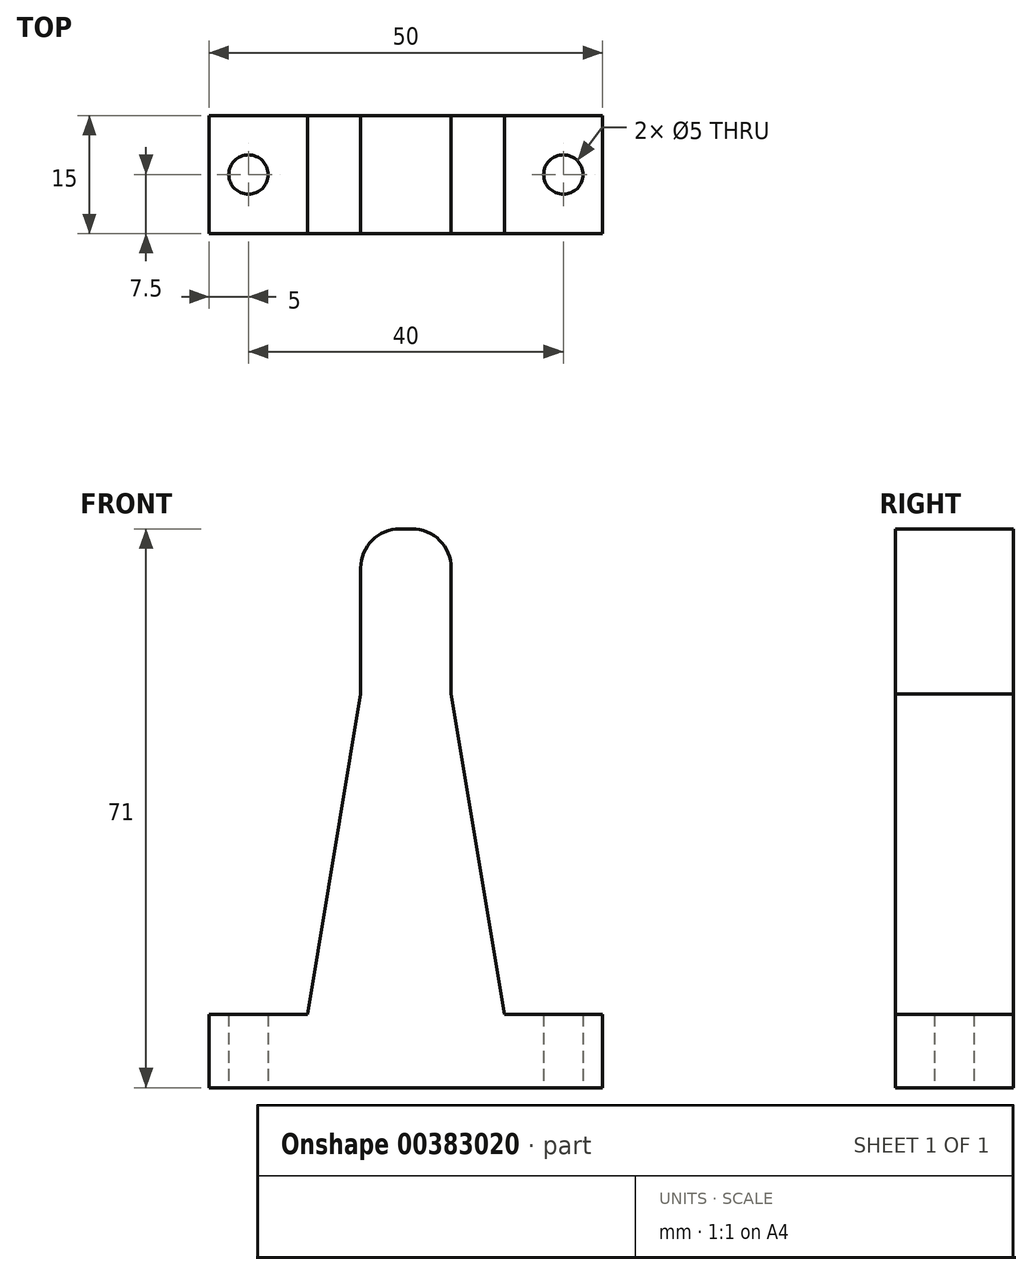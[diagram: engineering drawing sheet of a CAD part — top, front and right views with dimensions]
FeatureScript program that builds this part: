
annotation { "Feature Type Name" : "Feature", "Feature Type Description" : "" }
export const myFeature = defineFeature(function(context is Context, id is Id, definition is map)
    precondition{}
    {
        {
            var Q0;
            Q0=qCreatedBy(makeId("Front.planeOp"),FACE);
            var sketch = newSketch(context, id + "F0", { "sketchPlane" : qUnion([Q0])});
            skLineSegment(sketch, "E0.bottom", {"start": v(-0.75, 71) * mm, "end": v(0.75, 71) * mm});
            skLineSegment(sketch, "E0.top", {"start": v(-12.5, 0) * mm, "end": v(12.5, 0) * mm});
            skLineSegment(sketch, "E0.left", {"start": v(-12.5, 45) * mm, "end": v(-12.5, 9.28) * mm, "construction": true});
            skLineSegment(sketch, "E0.right", {"start": v(12.5, 44.18) * mm, "end": v(12.5, 9.28) * mm, "construction": true});
            skLineSegment(sketch, "E1.bottom", {"start": v(-25, 9.28) * mm, "end": v(-12.5, 9.28) * mm});
            skLineSegment(sketch, "E1.top", {"start": v(-25, 0) * mm, "end": v(25, 0) * mm});
            skLineSegment(sketch, "E1.left", {"start": v(-25, 9.28) * mm, "end": v(-25, 0) * mm});
            skLineSegment(sketch, "E1.right", {"start": v(25, 9.28) * mm, "end": v(25, 0) * mm});
            skLineSegment(sketch, "E2.trimOffspring", {"start": v(12.5, 9.28) * mm, "end": v(25, 9.28) * mm});
            skLineSegment(sketch, "E3", {"start": v(-5.75, 66) * mm, "end": v(-5.75, 50) * mm});
            skLineSegment(sketch, "E4", {"start": v(-10.75, 45) * mm, "end": v(-12.5, 45) * mm, "construction": true});
            skLineSegment(sketch, "E5", {"start": v(5.75, 66) * mm, "end": v(5.75, 50) * mm});
            skLineSegment(sketch, "E6", {"start": v(10.75, 45) * mm, "end": v(11.68, 45) * mm, "construction": true});
            skPoint(sketch, "E7.visualSharp", {"position": v(-5.75, 45) * mm});
            skArc(sketch, "E7.filletArc", {"start": v(-10.75, 45) * mm, "mid": v(-7.21, 46.46) * mm, "end": v(-5.75, 50) * mm, "construction": true});
            skPoint(sketch, "E8.visualSharp", {"position": v(5.75, 45) * mm});
            skArc(sketch, "E8.filletArc", {"start": v(5.75, 50) * mm, "mid": v(7.21, 46.46) * mm, "end": v(10.75, 45) * mm, "construction": true});
            skPoint(sketch, "E9.visualSharp", {"position": v(5.75, 71) * mm});
            skArc(sketch, "E9.filletArc", {"start": v(5.75, 66) * mm, "mid": v(4.29, 69.54) * mm, "end": v(0.75, 71) * mm});
            skPoint(sketch, "E10.visualSharp", {"position": v(-5.75, 71) * mm});
            skArc(sketch, "E10.filletArc", {"start": v(-0.75, 71) * mm, "mid": v(-4.29, 69.54) * mm, "end": v(-5.75, 66) * mm});
            skPoint(sketch, "E11.visualSharp", {"position": v(12.5, 45) * mm});
            skArc(sketch, "E11.filletArc", {"start": v(12.5, 44.18) * mm, "mid": v(12.26, 44.76) * mm, "end": v(11.68, 45) * mm, "construction": true});
            skLineSegment(sketch, "E12", {"start": v(-5.75, 50) * mm, "end": v(-12.5, 9.28) * mm});
            skLineSegment(sketch, "E13", {"start": v(5.75, 50) * mm, "end": v(12.5, 9.28) * mm});
            skSolve(sketch);
        }
        {
            var Q0;
            Q0 = qSketchRegion(id + "F0", true);
            extrude(context, id + "F1", {"entities" : qUnion([Q0]), "depth" : 15 * mm, "offsetDistance" : 25 * mm});
        }
        {
            var Q0;
            Q0=makeQuery(id+"F1.opExtrude","SWEPT_FACE",FACE,{"disambiguationData":[OSD([sQuery(id+"F0.wireOp",EDGE,"E1.top")])]});
            var sketch = newSketch(context, id + "F2", { "sketchPlane" : qUnion([Q0])});
            skLineSegment(sketch, "E14", {"start": v(-45.4, 7.5) * mm, "end": v(41.55, 7.5) * mm, "construction": true});
            skLineSegment(sketch, "E15.0.0", {"start": v(-25, 0) * mm, "end": v(25, 0) * mm, "construction": true});
            skLineSegment(sketch, "E15.0.1", {"start": v(25, 0) * mm, "end": v(25, 15) * mm, "construction": true});
            skLineSegment(sketch, "E15.0.2", {"start": v(25, 15) * mm, "end": v(-25, 15) * mm, "construction": true});
            skLineSegment(sketch, "E15.0.3", {"start": v(-25, 15) * mm, "end": v(-25, 0) * mm, "construction": true});
            skCircle(sketch, "E16", {"center": v(-20, 7.5) * mm, "radius": 2.5 * mm});
            skCircle(sketch, "E17", {"center": v(20, 7.5) * mm, "radius": 2.5 * mm});
            skSolve(sketch);
        }
        {
            var Q0;
            Q0 = qSketchRegion(id + "F2", true);
            extrude(context, id + "F3", {"entities" : qUnion([Q0]), "operationType" : NewBodyOperationType.REMOVE, "oppositeDirection" : true, "depth" : 25 * mm, "offsetDistance" : 25 * mm});
        }
    });
